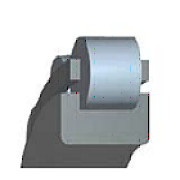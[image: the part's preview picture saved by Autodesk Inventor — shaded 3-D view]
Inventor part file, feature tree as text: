
AUTODESK INVENTOR PART (.ipt)
format: ipt  version: 2020 (Build 240168000, 168)  size: 164,864 bytes
history: native  units: mm (DEFAULTED — no unit token found)
features: sketch x1
ambient origin geometry x8: Origin, YZ Plane, XZ Plane, XY Plane, X Axis, Y Axis, Z Axis, Center Point
bodies: Solid1 (feature_tree), Body (feature_tree)
feature tree (1):
  sketch  "Sketch"  dims[d0=7.0mm d1=8.0mm d2=12.666667mm d3=22.0mm d4=90.0deg d5=0.3mm d6=0.0mm d7=0.0mm d8=0.0mm d9=0.0mm d10=0.0mm]
